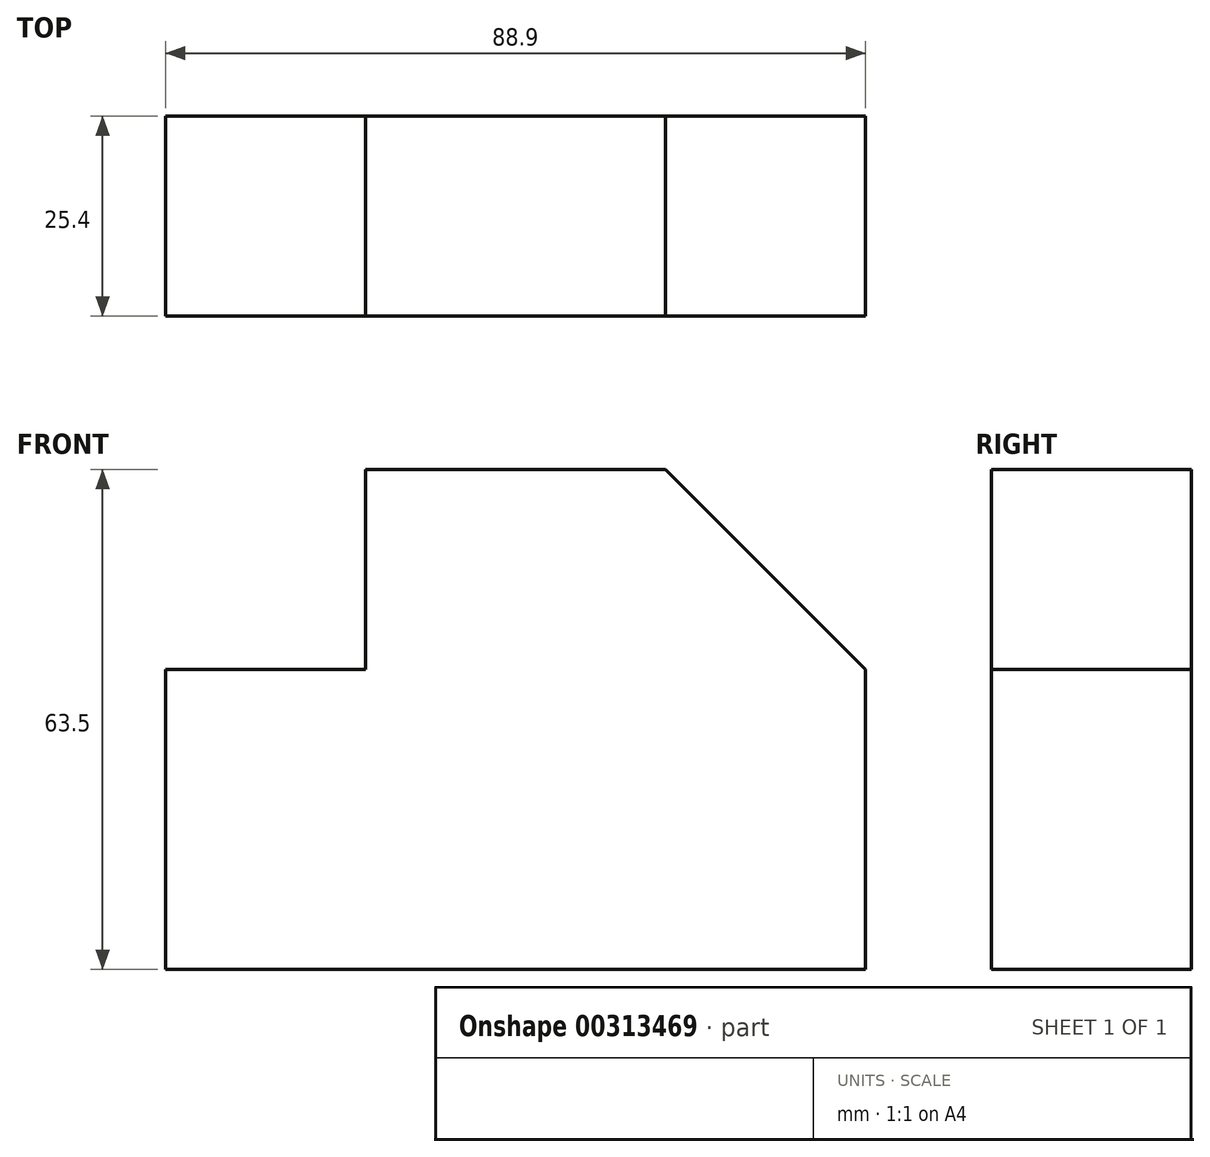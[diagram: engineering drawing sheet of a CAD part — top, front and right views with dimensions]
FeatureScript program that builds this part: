
annotation { "Feature Type Name" : "Feature", "Feature Type Description" : "" }
export const myFeature = defineFeature(function(context is Context, id is Id, definition is map)
    precondition{}
    {
        {
            var Q0;
            Q0=qCreatedBy(makeId("Front.planeOp"),FACE);
            var sketch = newSketch(context, id + "F0", { "sketchPlane" : qUnion([Q0])});
            skLineSegment(sketch, "E0", {"start": v(-51.08, -57.07) * mm, "end": v(37.82, -57.07) * mm});
            skLineSegment(sketch, "E1", {"start": v(37.82, -57.07) * mm, "end": v(37.82, -18.97) * mm});
            skLineSegment(sketch, "E2", {"start": v(37.82, -18.97) * mm, "end": v(12.42, 6.43) * mm});
            skLineSegment(sketch, "E3", {"start": v(12.42, 6.43) * mm, "end": v(-25.68, 6.43) * mm});
            skLineSegment(sketch, "E4", {"start": v(-25.68, 6.43) * mm, "end": v(-25.68, -18.97) * mm});
            skLineSegment(sketch, "E5", {"start": v(-25.68, -18.97) * mm, "end": v(-51.08, -18.97) * mm});
            skLineSegment(sketch, "E6", {"start": v(-51.08, -18.97) * mm, "end": v(-51.08, -57.07) * mm});
            skSolve(sketch);
        }
        {
            var Q0;
            Q0 = qSketchRegion(id + "F0", true);
            extrude(context, id + "F1", {"entities" : qUnion([Q0]), "depth" : 25.4 * mm});
        }
    });
